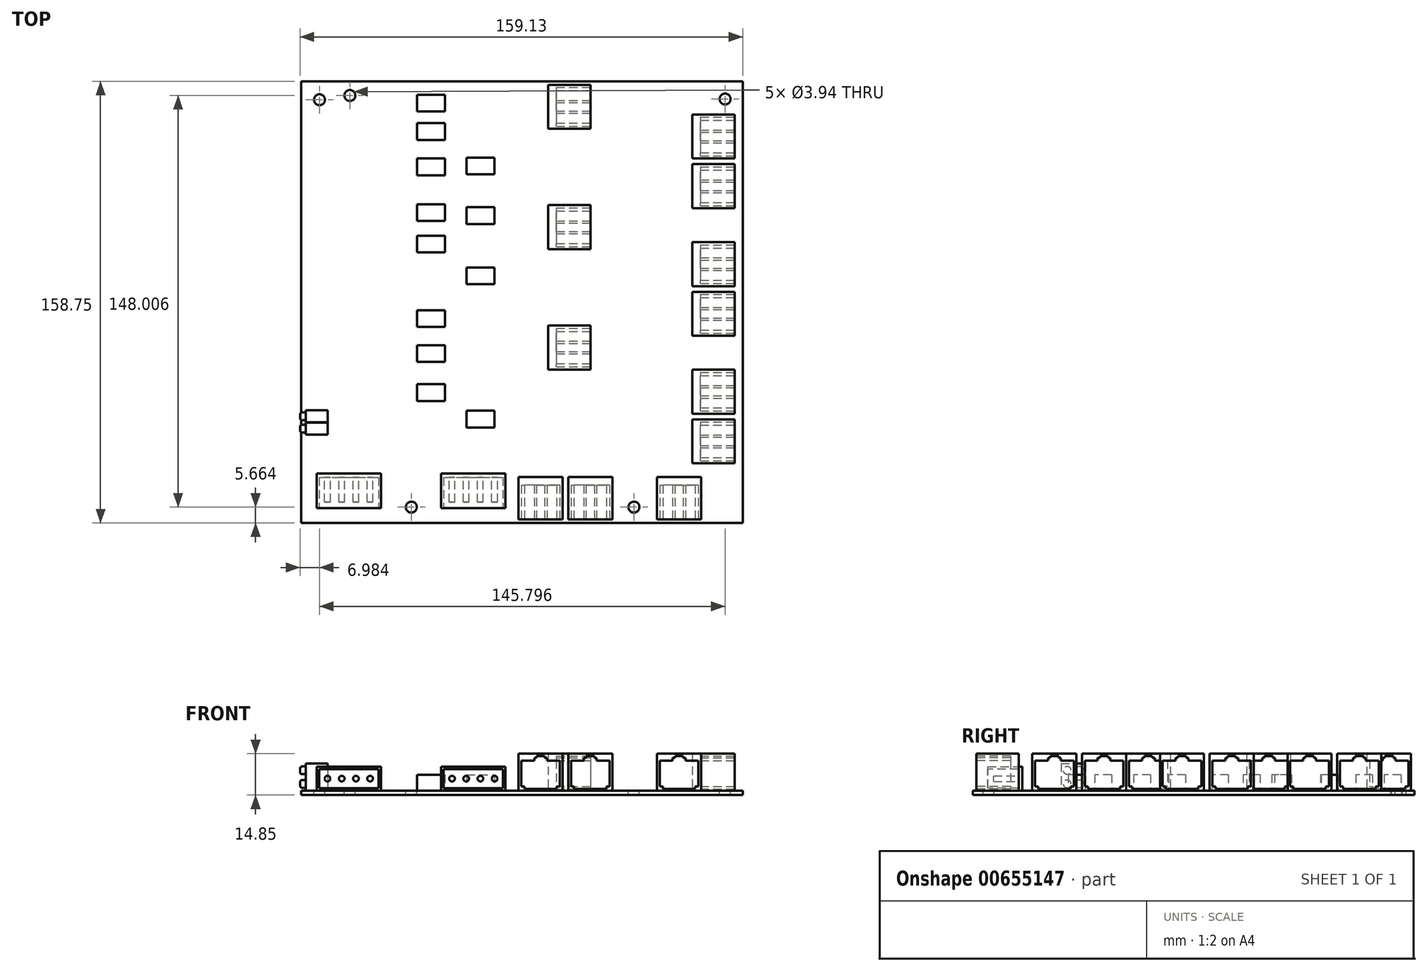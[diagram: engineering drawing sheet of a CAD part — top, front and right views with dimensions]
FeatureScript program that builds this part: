
annotation { "Feature Type Name" : "Feature", "Feature Type Description" : "" }
export const myFeature = defineFeature(function(context is Context, id is Id, definition is map)
    precondition{}
    {
        {
            var Q0;
            Q0=qCreatedBy(makeId("Top.planeOp"),FACE);
            var sketch = newSketch(context, id + "F0", { "sketchPlane" : qUnion([Q0])});
            skLineSegment(sketch, "E0.bottom", {"start": v(0, 0) * mm, "end": v(158.75, 0) * mm});
            skLineSegment(sketch, "E0.top", {"start": v(0, 158.75) * mm, "end": v(158.75, 158.75) * mm});
            skLineSegment(sketch, "E0.left", {"start": v(0, 0) * mm, "end": v(0, 158.75) * mm});
            skLineSegment(sketch, "E0.right", {"start": v(158.75, 0) * mm, "end": v(158.75, 158.75) * mm});
            skSolve(sketch);
        }
        {
            var Q0;
            Q0=makeQuery(id+"F0.imprint","IMPRINT",FACE,{"disambiguationData":[TD([[makeQuery(id+"F0.imprint","IMPRINT",EDGE,{"derivedFrom":sQuery(id+"F0.wireOp",EDGE,"E0.bottom")}),1.0]])]});
            extrude(context, id + "F1", {"entities" : qUnion([Q0]), "depth" : 1.59 * mm, "offsetDistance" : 25.4 * mm});
        }
        {
            var Q0;
            Q0=makeQuery(id+"F1.opExtrude","CAP_FACE",FACE,{"disambiguationData":[OSD([sQuery(id+"F0.wireOp",EDGE,"E0.bottom"),sQuery(id+"F0.wireOp",EDGE,"E0.top"),sQuery(id+"F0.wireOp",EDGE,"E0.left"),sQuery(id+"F0.wireOp",EDGE,"E0.right")])],"isStart":false});
            var sketch = newSketch(context, id + "F2", { "sketchPlane" : qUnion([Q0])});
            skCircle(sketch, "E1", {"center": v(119.63, 5.66) * mm, "radius": 1.97 * mm});
            skCircle(sketch, "E2", {"center": v(39.62, 5.66) * mm, "radius": 1.97 * mm});
            skCircle(sketch, "E3", {"center": v(152.4, 152.4) * mm, "radius": 1.97 * mm});
            skCircle(sketch, "E4", {"center": v(17.53, 153.67) * mm, "radius": 1.97 * mm});
            skCircle(sketch, "E5", {"center": v(6.6, 152.15) * mm, "radius": 1.97 * mm});
            skSolve(sketch);
        }
        {
            var Q0;
            Q0 = qSketchRegion(id + "F2", true);
            extrude(context, id + "F3", {"entities" : qUnion([Q0]), "operationType" : NewBodyOperationType.REMOVE, "endBound" : BoundingType.UP_TO_NEXT, "oppositeDirection" : true, "depth" : 25.4 * mm, "offsetDistance" : 25.4 * mm});
        }
        {
            var Q0;
            Q0=makeQuery(id+"F1.opExtrude","CAP_FACE",FACE,{"disambiguationData":[OSD([sQuery(id+"F0.wireOp",EDGE,"E0.bottom"),sQuery(id+"F0.wireOp",EDGE,"E0.top"),sQuery(id+"F0.wireOp",EDGE,"E0.left"),sQuery(id+"F0.wireOp",EDGE,"E0.right")])],"isStart":false});
            var sketch = newSketch(context, id + "F4", { "sketchPlane" : qUnion([Q0])});
            skLineSegment(sketch, "E6.bottom", {"start": v(140.61, 21.39) * mm, "end": v(155.85, 21.39) * mm});
            skLineSegment(sketch, "E6.top", {"start": v(140.61, 37.21) * mm, "end": v(155.85, 37.21) * mm});
            skLineSegment(sketch, "E6.left", {"start": v(140.61, 21.39) * mm, "end": v(140.61, 37.21) * mm});
            skLineSegment(sketch, "E6.right", {"start": v(155.85, 21.39) * mm, "end": v(155.85, 37.21) * mm});
            skLineSegment(sketch, "E7.bottom", {"start": v(140.61, 39.24) * mm, "end": v(155.85, 39.24) * mm});
            skLineSegment(sketch, "E7.top", {"start": v(140.61, 55.07) * mm, "end": v(155.85, 55.07) * mm});
            skLineSegment(sketch, "E7.left", {"start": v(140.61, 39.24) * mm, "end": v(140.61, 55.07) * mm});
            skLineSegment(sketch, "E7.right", {"start": v(155.85, 39.24) * mm, "end": v(155.85, 55.07) * mm});
            skLineSegment(sketch, "E8.bottom", {"start": v(140.61, 67.26) * mm, "end": v(155.85, 67.26) * mm});
            skLineSegment(sketch, "E8.top", {"start": v(140.61, 83.08) * mm, "end": v(155.85, 83.08) * mm});
            skLineSegment(sketch, "E8.left", {"start": v(140.61, 67.26) * mm, "end": v(140.61, 83.08) * mm});
            skLineSegment(sketch, "E8.right", {"start": v(155.85, 67.26) * mm, "end": v(155.85, 83.08) * mm});
            skLineSegment(sketch, "E9.bottom", {"start": v(140.61, 85.12) * mm, "end": v(155.85, 85.12) * mm});
            skLineSegment(sketch, "E9.top", {"start": v(140.61, 100.94) * mm, "end": v(155.85, 100.94) * mm});
            skLineSegment(sketch, "E9.left", {"start": v(140.61, 85.12) * mm, "end": v(140.61, 100.94) * mm});
            skLineSegment(sketch, "E9.right", {"start": v(155.85, 85.12) * mm, "end": v(155.85, 100.94) * mm});
            skLineSegment(sketch, "E10.bottom", {"start": v(140.61, 113.13) * mm, "end": v(155.85, 113.13) * mm});
            skLineSegment(sketch, "E10.top", {"start": v(140.61, 128.96) * mm, "end": v(155.85, 128.96) * mm});
            skLineSegment(sketch, "E10.left", {"start": v(140.61, 113.13) * mm, "end": v(140.61, 128.96) * mm});
            skLineSegment(sketch, "E10.right", {"start": v(155.85, 113.13) * mm, "end": v(155.85, 128.96) * mm});
            skLineSegment(sketch, "E11.bottom", {"start": v(140.61, 130.99) * mm, "end": v(155.85, 130.99) * mm});
            skLineSegment(sketch, "E11.top", {"start": v(140.61, 146.81) * mm, "end": v(155.85, 146.81) * mm});
            skLineSegment(sketch, "E11.left", {"start": v(140.61, 130.99) * mm, "end": v(140.61, 146.81) * mm});
            skLineSegment(sketch, "E11.right", {"start": v(155.85, 130.99) * mm, "end": v(155.85, 146.81) * mm});
            skLineSegment(sketch, "E12.bottom", {"start": v(127.94, 1.27) * mm, "end": v(143.76, 1.27) * mm});
            skLineSegment(sketch, "E12.top", {"start": v(127.94, 16.51) * mm, "end": v(143.76, 16.51) * mm});
            skLineSegment(sketch, "E12.left", {"start": v(127.94, 1.27) * mm, "end": v(127.94, 16.51) * mm});
            skLineSegment(sketch, "E12.right", {"start": v(143.76, 1.27) * mm, "end": v(143.76, 16.51) * mm});
            skLineSegment(sketch, "E13.bottom", {"start": v(111.86, 1.27) * mm, "end": v(96.04, 1.27) * mm});
            skLineSegment(sketch, "E13.top", {"start": v(111.86, 16.51) * mm, "end": v(96.04, 16.51) * mm});
            skLineSegment(sketch, "E13.left", {"start": v(111.86, 1.27) * mm, "end": v(111.86, 16.51) * mm});
            skLineSegment(sketch, "E13.right", {"start": v(96.04, 1.27) * mm, "end": v(96.04, 16.51) * mm});
            skLineSegment(sketch, "E14.bottom", {"start": v(94, 1.27) * mm, "end": v(78.18, 1.27) * mm});
            skLineSegment(sketch, "E14.top", {"start": v(94, 16.51) * mm, "end": v(78.18, 16.51) * mm});
            skLineSegment(sketch, "E14.left", {"start": v(94, 1.27) * mm, "end": v(94, 16.51) * mm});
            skLineSegment(sketch, "E14.right", {"start": v(78.18, 1.27) * mm, "end": v(78.18, 16.51) * mm});
            skLineSegment(sketch, "E15.bottom", {"start": v(88.82, 157.48) * mm, "end": v(104.06, 157.48) * mm});
            skLineSegment(sketch, "E15.top", {"start": v(88.82, 141.66) * mm, "end": v(104.06, 141.66) * mm});
            skLineSegment(sketch, "E15.left", {"start": v(88.82, 157.48) * mm, "end": v(88.82, 141.66) * mm});
            skLineSegment(sketch, "E15.right", {"start": v(104.06, 157.48) * mm, "end": v(104.06, 141.66) * mm});
            skLineSegment(sketch, "E16.bottom", {"start": v(88.82, 114.22) * mm, "end": v(104.06, 114.22) * mm});
            skLineSegment(sketch, "E16.top", {"start": v(88.82, 98.4) * mm, "end": v(104.06, 98.4) * mm});
            skLineSegment(sketch, "E16.left", {"start": v(88.82, 114.22) * mm, "end": v(88.82, 98.4) * mm});
            skLineSegment(sketch, "E16.right", {"start": v(104.06, 114.22) * mm, "end": v(104.06, 98.4) * mm});
            skLineSegment(sketch, "E17.bottom", {"start": v(88.82, 70.97) * mm, "end": v(104.06, 70.97) * mm});
            skLineSegment(sketch, "E17.top", {"start": v(88.82, 55.14) * mm, "end": v(104.06, 55.14) * mm});
            skLineSegment(sketch, "E17.left", {"start": v(88.82, 70.97) * mm, "end": v(88.82, 55.14) * mm});
            skLineSegment(sketch, "E17.right", {"start": v(104.06, 70.97) * mm, "end": v(104.06, 55.14) * mm});
            skSolve(sketch);
        }
        {
            var Q0;
            Q0 = qSketchRegion(id + "F4", true);
            extrude(context, id + "F5", {"entities" : qUnion([Q0]), "operationType" : NewBodyOperationType.ADD, "depth" : 13.26 * mm, "offsetDistance" : 25.4 * mm});
        }
        {
            var Q0;
            Q0=makeQuery(id+"F5.opExtrude","SWEPT_FACE",FACE,{"disambiguationData":[OSD([sQuery(id+"F4.wireOp",EDGE,"E6.right")])]});
            var sketch = newSketch(context, id + "F6", { "sketchPlane" : qUnion([Q0])});
            skLineSegment(sketch, "E18", {"start": v(29.3, 13.98) * mm, "end": v(30.79, 13.98) * mm});
            skPoint(sketch, "E18.startSnap0", {"position": v(29.3, 14.85) * mm});
            skLineSegment(sketch, "E19", {"start": v(30.79, 13.98) * mm, "end": v(30.79, 13.32) * mm});
            skLineSegment(sketch, "E20", {"start": v(30.79, 13.32) * mm, "end": v(31.6, 13.32) * mm});
            skLineSegment(sketch, "E21", {"start": v(31.6, 13.32) * mm, "end": v(31.6, 12.4) * mm});
            skLineSegment(sketch, "E22", {"start": v(31.6, 12.4) * mm, "end": v(36.25, 12.4) * mm});
            skLineSegment(sketch, "E23", {"start": v(36.25, 12.4) * mm, "end": v(36.25, 3.14) * mm});
            skLineSegment(sketch, "E24", {"start": v(36.25, 3.14) * mm, "end": v(35.12, 3.14) * mm});
            skLineSegment(sketch, "E25", {"start": v(35.12, 3.14) * mm, "end": v(35.12, 2.16) * mm});
            skLineSegment(sketch, "E26", {"start": v(35.12, 2.16) * mm, "end": v(29.3, 2.16) * mm});
            skLineSegment(sketch, "E27.MirrorCS", {"start": v(23.47, 3.14) * mm, "end": v(23.47, 2.16) * mm});
            skLineSegment(sketch, "E28.MirrorCS", {"start": v(22.35, 3.14) * mm, "end": v(23.47, 3.14) * mm});
            skLineSegment(sketch, "E29.MirrorCS", {"start": v(27, 13.32) * mm, "end": v(27, 12.4) * mm});
            skLineSegment(sketch, "E30.MirrorCS", {"start": v(27.8, 13.32) * mm, "end": v(27, 13.32) * mm});
            skLineSegment(sketch, "E31.MirrorCS", {"start": v(27.8, 13.98) * mm, "end": v(27.8, 13.32) * mm});
            skLineSegment(sketch, "E32.MirrorCS", {"start": v(23.47, 2.16) * mm, "end": v(29.3, 2.16) * mm});
            skLineSegment(sketch, "E33.MirrorCS", {"start": v(22.35, 12.4) * mm, "end": v(22.35, 3.14) * mm});
            skLineSegment(sketch, "E34.MirrorCS", {"start": v(29.3, 13.98) * mm, "end": v(27.8, 13.98) * mm});
            skLineSegment(sketch, "E35.MirrorCS", {"start": v(27, 12.4) * mm, "end": v(22.35, 12.4) * mm});
            skSolve(sketch);
        }
        {
            var Q0;
            Q0=makeQuery(id+"F6.imprint","IMPRINT",FACE,{"disambiguationData":[TD([[makeQuery(id+"F6.imprint","IMPRINT",EDGE,{"derivedFrom":sQuery(id+"F6.wireOp",EDGE,"E18")}),-1.0]])]});
            extrude(context, id + "F7", {"entities" : qUnion([Q0]), "operationType" : NewBodyOperationType.REMOVE, "oppositeDirection" : true, "depth" : 12.32 * mm, "offsetDistance" : 25.4 * mm});
        }
        {
            var Q0;
            Q0=makeQuery(id+"F5.opExtrude","SWEPT_FACE",FACE,{"disambiguationData":[OSD([sQuery(id+"F4.wireOp",EDGE,"E7.right")])]});
            var sketch = newSketch(context, id + "F8", { "sketchPlane" : qUnion([Q0])});
            skLineSegment(sketch, "E36", {"start": v(47.16, 13.98) * mm, "end": v(48.64, 13.98) * mm});
            skPoint(sketch, "E36.startSnap0", {"position": v(47.16, 14.85) * mm});
            skLineSegment(sketch, "E37", {"start": v(48.64, 13.98) * mm, "end": v(48.64, 13.32) * mm});
            skLineSegment(sketch, "E38", {"start": v(48.64, 13.32) * mm, "end": v(49.45, 13.32) * mm});
            skLineSegment(sketch, "E39", {"start": v(49.45, 13.32) * mm, "end": v(49.45, 12.4) * mm});
            skLineSegment(sketch, "E40", {"start": v(49.45, 12.4) * mm, "end": v(54.1, 12.4) * mm});
            skLineSegment(sketch, "E41", {"start": v(54.1, 12.4) * mm, "end": v(54.1, 3.14) * mm});
            skLineSegment(sketch, "E42", {"start": v(54.1, 3.14) * mm, "end": v(52.98, 3.14) * mm});
            skLineSegment(sketch, "E43", {"start": v(52.98, 3.14) * mm, "end": v(52.98, 2.16) * mm});
            skLineSegment(sketch, "E44", {"start": v(52.98, 2.16) * mm, "end": v(47.16, 2.16) * mm});
            skPoint(sketch, "E45.endSnap0", {"position": v(47.16, 1.59) * mm});
            skLineSegment(sketch, "E46.MirrorCS", {"start": v(41.33, 2.16) * mm, "end": v(47.16, 2.16) * mm});
            skLineSegment(sketch, "E47.MirrorCS", {"start": v(41.33, 3.14) * mm, "end": v(41.33, 2.16) * mm});
            skLineSegment(sketch, "E48.MirrorCS", {"start": v(44.86, 12.4) * mm, "end": v(40.2, 12.4) * mm});
            skLineSegment(sketch, "E49.MirrorCS", {"start": v(44.86, 13.32) * mm, "end": v(44.86, 12.4) * mm});
            skLineSegment(sketch, "E50.MirrorCS", {"start": v(47.16, 13.98) * mm, "end": v(45.67, 13.98) * mm});
            skLineSegment(sketch, "E51.MirrorCS", {"start": v(45.67, 13.98) * mm, "end": v(45.67, 13.32) * mm});
            skLineSegment(sketch, "E52.MirrorCS", {"start": v(45.67, 13.32) * mm, "end": v(44.86, 13.32) * mm});
            skLineSegment(sketch, "E53.MirrorCS", {"start": v(40.2, 12.4) * mm, "end": v(40.2, 3.14) * mm});
            skLineSegment(sketch, "E54.MirrorCS", {"start": v(40.2, 3.14) * mm, "end": v(41.33, 3.14) * mm});
            skLineSegment(sketch, "E55", {"start": v(73.68, 13.98) * mm, "end": v(76.66, 13.98) * mm});
            skPoint(sketch, "E55.startSnap0", {"position": v(75.17, 14.85) * mm});
            skLineSegment(sketch, "E56", {"start": v(76.66, 13.98) * mm, "end": v(76.66, 13.32) * mm});
            skLineSegment(sketch, "E57", {"start": v(76.66, 13.32) * mm, "end": v(77.47, 13.32) * mm});
            skLineSegment(sketch, "E58", {"start": v(77.47, 13.32) * mm, "end": v(77.47, 12.4) * mm});
            skLineSegment(sketch, "E59", {"start": v(77.47, 12.4) * mm, "end": v(82.12, 12.4) * mm});
            skLineSegment(sketch, "E60", {"start": v(82.12, 12.4) * mm, "end": v(82.12, 3.14) * mm});
            skLineSegment(sketch, "E61", {"start": v(82.12, 3.14) * mm, "end": v(81, 3.14) * mm});
            skLineSegment(sketch, "E62", {"start": v(81, 3.14) * mm, "end": v(81, 2.16) * mm});
            skLineSegment(sketch, "E63", {"start": v(81, 2.16) * mm, "end": v(69.35, 2.16) * mm});
            skPoint(sketch, "E64.endSnap0", {"position": v(75.91, 1.22) * mm});
            skLineSegment(sketch, "E65.MirrorCS", {"start": v(69.35, 3.14) * mm, "end": v(69.35, 2.16) * mm});
            skLineSegment(sketch, "E66.MirrorCS", {"start": v(72.87, 12.4) * mm, "end": v(68.22, 12.4) * mm});
            skLineSegment(sketch, "E67.MirrorCS", {"start": v(72.87, 13.32) * mm, "end": v(72.87, 12.4) * mm});
            skLineSegment(sketch, "E68.MirrorCS", {"start": v(73.68, 13.98) * mm, "end": v(73.68, 13.32) * mm});
            skLineSegment(sketch, "E69.MirrorCS", {"start": v(73.68, 13.32) * mm, "end": v(72.87, 13.32) * mm});
            skLineSegment(sketch, "E70.MirrorCS", {"start": v(68.22, 12.4) * mm, "end": v(68.22, 3.14) * mm});
            skLineSegment(sketch, "E71.MirrorCS", {"start": v(68.22, 3.14) * mm, "end": v(69.35, 3.14) * mm});
            skPoint(sketch, "E72.orphan", {"position": v(75.17, 13.98) * mm});
            skPoint(sketch, "E73.orphan", {"position": v(75.17, 2.16) * mm});
            skLineSegment(sketch, "E74", {"start": v(91.54, 13.98) * mm, "end": v(94.52, 13.98) * mm});
            skPoint(sketch, "E74.startSnap0", {"position": v(93.03, 14.85) * mm});
            skLineSegment(sketch, "E75", {"start": v(94.52, 13.98) * mm, "end": v(94.52, 13.32) * mm});
            skLineSegment(sketch, "E76", {"start": v(94.52, 13.32) * mm, "end": v(95.32, 13.32) * mm});
            skLineSegment(sketch, "E77", {"start": v(95.32, 13.32) * mm, "end": v(95.32, 12.4) * mm});
            skLineSegment(sketch, "E78", {"start": v(95.32, 12.4) * mm, "end": v(99.98, 12.4) * mm});
            skLineSegment(sketch, "E79", {"start": v(99.98, 12.4) * mm, "end": v(99.98, 3.14) * mm});
            skLineSegment(sketch, "E80", {"start": v(99.98, 3.14) * mm, "end": v(98.85, 3.14) * mm});
            skLineSegment(sketch, "E81", {"start": v(98.85, 3.14) * mm, "end": v(98.85, 2.16) * mm});
            skLineSegment(sketch, "E82", {"start": v(98.85, 2.16) * mm, "end": v(87.2, 2.16) * mm});
            skLineSegment(sketch, "E83.MirrorCS", {"start": v(87.2, 3.14) * mm, "end": v(87.2, 2.16) * mm});
            skLineSegment(sketch, "E84.MirrorCS", {"start": v(90.73, 12.4) * mm, "end": v(86.08, 12.4) * mm});
            skLineSegment(sketch, "E85.MirrorCS", {"start": v(90.73, 13.32) * mm, "end": v(90.73, 12.4) * mm});
            skLineSegment(sketch, "E86.MirrorCS", {"start": v(91.54, 13.98) * mm, "end": v(91.54, 13.32) * mm});
            skLineSegment(sketch, "E87.MirrorCS", {"start": v(91.54, 13.32) * mm, "end": v(90.73, 13.32) * mm});
            skLineSegment(sketch, "E88.MirrorCS", {"start": v(86.08, 12.4) * mm, "end": v(86.08, 3.14) * mm});
            skLineSegment(sketch, "E89.MirrorCS", {"start": v(86.08, 3.14) * mm, "end": v(87.2, 3.14) * mm});
            skPoint(sketch, "E90.orphan", {"position": v(93.03, 13.98) * mm});
            skPoint(sketch, "E91.orphan", {"position": v(93.03, 2.16) * mm});
            skLineSegment(sketch, "E92", {"start": v(119.55, 13.98) * mm, "end": v(122.53, 13.98) * mm});
            skPoint(sketch, "E92.startSnap0", {"position": v(121.04, 14.85) * mm});
            skLineSegment(sketch, "E93", {"start": v(122.53, 13.98) * mm, "end": v(122.53, 13.32) * mm});
            skLineSegment(sketch, "E94", {"start": v(122.53, 13.32) * mm, "end": v(123.34, 13.32) * mm});
            skLineSegment(sketch, "E95", {"start": v(123.34, 13.32) * mm, "end": v(123.34, 12.4) * mm});
            skLineSegment(sketch, "E96", {"start": v(123.34, 12.4) * mm, "end": v(128, 12.4) * mm});
            skLineSegment(sketch, "E97", {"start": v(128, 12.4) * mm, "end": v(128, 3.14) * mm});
            skLineSegment(sketch, "E98", {"start": v(128, 3.14) * mm, "end": v(126.87, 3.14) * mm});
            skLineSegment(sketch, "E99", {"start": v(126.87, 3.14) * mm, "end": v(126.87, 2.16) * mm});
            skLineSegment(sketch, "E100", {"start": v(126.87, 2.16) * mm, "end": v(115.22, 2.16) * mm});
            skLineSegment(sketch, "E101.MirrorCS", {"start": v(115.22, 3.14) * mm, "end": v(115.22, 2.16) * mm});
            skLineSegment(sketch, "E102.MirrorCS", {"start": v(118.75, 12.4) * mm, "end": v(114.1, 12.4) * mm});
            skLineSegment(sketch, "E103.MirrorCS", {"start": v(118.75, 13.32) * mm, "end": v(118.75, 12.4) * mm});
            skLineSegment(sketch, "E104.MirrorCS", {"start": v(119.55, 13.98) * mm, "end": v(119.55, 13.32) * mm});
            skLineSegment(sketch, "E105.MirrorCS", {"start": v(119.55, 13.32) * mm, "end": v(118.75, 13.32) * mm});
            skLineSegment(sketch, "E106.MirrorCS", {"start": v(114.1, 12.4) * mm, "end": v(114.1, 3.14) * mm});
            skLineSegment(sketch, "E107.MirrorCS", {"start": v(114.1, 3.14) * mm, "end": v(115.22, 3.14) * mm});
            skPoint(sketch, "E108.orphan", {"position": v(121.04, 13.98) * mm});
            skPoint(sketch, "E109.orphan", {"position": v(121.04, 2.16) * mm});
            skLineSegment(sketch, "E110", {"start": v(137.41, 13.98) * mm, "end": v(140.39, 13.98) * mm});
            skPoint(sketch, "E110.startSnap0", {"position": v(138.9, 14.85) * mm});
            skLineSegment(sketch, "E111", {"start": v(140.39, 13.98) * mm, "end": v(140.39, 13.32) * mm});
            skLineSegment(sketch, "E112", {"start": v(140.39, 13.32) * mm, "end": v(141.2, 13.32) * mm});
            skLineSegment(sketch, "E113", {"start": v(141.2, 13.32) * mm, "end": v(141.2, 12.4) * mm});
            skLineSegment(sketch, "E114", {"start": v(141.2, 12.4) * mm, "end": v(145.85, 12.4) * mm});
            skLineSegment(sketch, "E115", {"start": v(145.85, 12.4) * mm, "end": v(145.85, 3.14) * mm});
            skLineSegment(sketch, "E116", {"start": v(145.85, 3.14) * mm, "end": v(144.72, 3.14) * mm});
            skLineSegment(sketch, "E117", {"start": v(144.72, 3.14) * mm, "end": v(144.72, 2.16) * mm});
            skLineSegment(sketch, "E118", {"start": v(144.72, 2.16) * mm, "end": v(133.08, 2.16) * mm});
            skPoint(sketch, "E119.endSnap0", {"position": v(145.22, -24.66) * mm});
            skLineSegment(sketch, "E120.MirrorCS", {"start": v(133.08, 3.14) * mm, "end": v(133.08, 2.16) * mm});
            skLineSegment(sketch, "E121.MirrorCS", {"start": v(136.6, 12.4) * mm, "end": v(131.95, 12.4) * mm});
            skLineSegment(sketch, "E122.MirrorCS", {"start": v(136.6, 13.32) * mm, "end": v(136.6, 12.4) * mm});
            skLineSegment(sketch, "E123.MirrorCS", {"start": v(137.41, 13.98) * mm, "end": v(137.41, 13.32) * mm});
            skLineSegment(sketch, "E124.MirrorCS", {"start": v(137.41, 13.32) * mm, "end": v(136.6, 13.32) * mm});
            skLineSegment(sketch, "E125.MirrorCS", {"start": v(131.95, 12.4) * mm, "end": v(131.95, 3.14) * mm});
            skLineSegment(sketch, "E126.MirrorCS", {"start": v(131.95, 3.14) * mm, "end": v(133.08, 3.14) * mm});
            skPoint(sketch, "E127.orphan", {"position": v(138.9, 13.98) * mm});
            skPoint(sketch, "E128.orphan", {"position": v(138.9, 2.16) * mm});
            skSolve(sketch);
        }
        {
            var Q0;
            Q0 = qSketchRegion(id + "F8", true);
            extrude(context, id + "F9", {"entities" : qUnion([Q0]), "operationType" : NewBodyOperationType.REMOVE, "oppositeDirection" : true, "depth" : 12.32 * mm, "offsetDistance" : 25.4 * mm});
        }
        {
            var Q0;
            Q0=makeQuery(id+"F5.opExtrude","SWEPT_FACE",FACE,{"disambiguationData":[OSD([sQuery(id+"F4.wireOp",EDGE,"E17.right")])]});
            var sketch = newSketch(context, id + "F10", { "sketchPlane" : qUnion([Q0])});
            skLineSegment(sketch, "E129", {"start": v(61.57, 13.98) * mm, "end": v(64.54, 13.98) * mm});
            skPoint(sketch, "E129.startSnap0", {"position": v(63.06, 14.85) * mm});
            skLineSegment(sketch, "E130", {"start": v(64.54, 13.98) * mm, "end": v(64.54, 13.32) * mm});
            skLineSegment(sketch, "E131", {"start": v(64.54, 13.32) * mm, "end": v(65.35, 13.32) * mm});
            skLineSegment(sketch, "E132", {"start": v(65.35, 13.32) * mm, "end": v(65.35, 12.4) * mm});
            skLineSegment(sketch, "E133", {"start": v(65.35, 12.4) * mm, "end": v(70, 12.4) * mm});
            skLineSegment(sketch, "E134", {"start": v(70, 12.4) * mm, "end": v(70, 3.14) * mm});
            skLineSegment(sketch, "E135", {"start": v(70, 3.14) * mm, "end": v(68.88, 3.14) * mm});
            skLineSegment(sketch, "E136", {"start": v(68.88, 3.14) * mm, "end": v(68.88, 2.16) * mm});
            skLineSegment(sketch, "E137", {"start": v(68.88, 2.16) * mm, "end": v(57.23, 2.16) * mm});
            skLineSegment(sketch, "E138.MirrorCS", {"start": v(57.23, 3.14) * mm, "end": v(57.23, 2.16) * mm});
            skLineSegment(sketch, "E139.MirrorCS", {"start": v(60.76, 12.4) * mm, "end": v(56.1, 12.4) * mm});
            skLineSegment(sketch, "E140.MirrorCS", {"start": v(60.76, 13.32) * mm, "end": v(60.76, 12.4) * mm});
            skLineSegment(sketch, "E141.MirrorCS", {"start": v(61.57, 13.98) * mm, "end": v(61.57, 13.32) * mm});
            skLineSegment(sketch, "E142.MirrorCS", {"start": v(61.57, 13.32) * mm, "end": v(60.76, 13.32) * mm});
            skLineSegment(sketch, "E143.MirrorCS", {"start": v(56.1, 12.4) * mm, "end": v(56.1, 3.14) * mm});
            skLineSegment(sketch, "E144.MirrorCS", {"start": v(56.1, 3.14) * mm, "end": v(57.23, 3.14) * mm});
            skPoint(sketch, "E145.orphan", {"position": v(63.06, 13.98) * mm});
            skPoint(sketch, "E146.orphan", {"position": v(63.06, 2.16) * mm});
            skLineSegment(sketch, "E147", {"start": v(104.82, 13.98) * mm, "end": v(107.8, 13.98) * mm});
            skPoint(sketch, "E147.startSnap0", {"position": v(106.31, 14.85) * mm});
            skLineSegment(sketch, "E148", {"start": v(107.8, 13.98) * mm, "end": v(107.8, 13.32) * mm});
            skLineSegment(sketch, "E149", {"start": v(107.8, 13.32) * mm, "end": v(108.6, 13.32) * mm});
            skLineSegment(sketch, "E150", {"start": v(108.6, 13.32) * mm, "end": v(108.6, 12.4) * mm});
            skLineSegment(sketch, "E151", {"start": v(108.6, 12.4) * mm, "end": v(113.26, 12.4) * mm});
            skLineSegment(sketch, "E152", {"start": v(113.26, 12.4) * mm, "end": v(113.26, 3.14) * mm});
            skLineSegment(sketch, "E153", {"start": v(113.26, 3.14) * mm, "end": v(112.14, 3.14) * mm});
            skLineSegment(sketch, "E154", {"start": v(112.14, 3.14) * mm, "end": v(112.14, 2.16) * mm});
            skLineSegment(sketch, "E155", {"start": v(112.14, 2.16) * mm, "end": v(100.49, 2.16) * mm});
            skLineSegment(sketch, "E156.MirrorCS", {"start": v(100.49, 3.14) * mm, "end": v(100.49, 2.16) * mm});
            skLineSegment(sketch, "E157.MirrorCS", {"start": v(104.02, 12.4) * mm, "end": v(99.36, 12.4) * mm});
            skLineSegment(sketch, "E158.MirrorCS", {"start": v(104.02, 13.32) * mm, "end": v(104.02, 12.4) * mm});
            skLineSegment(sketch, "E159.MirrorCS", {"start": v(104.82, 13.98) * mm, "end": v(104.82, 13.32) * mm});
            skLineSegment(sketch, "E160.MirrorCS", {"start": v(104.82, 13.32) * mm, "end": v(104.02, 13.32) * mm});
            skLineSegment(sketch, "E161.MirrorCS", {"start": v(99.36, 12.4) * mm, "end": v(99.36, 3.14) * mm});
            skLineSegment(sketch, "E162.MirrorCS", {"start": v(99.36, 3.14) * mm, "end": v(100.49, 3.14) * mm});
            skPoint(sketch, "E163.orphan", {"position": v(106.31, 13.98) * mm});
            skPoint(sketch, "E164.orphan", {"position": v(106.31, 2.16) * mm});
            skLineSegment(sketch, "E165", {"start": v(148.08, 13.98) * mm, "end": v(151.06, 13.98) * mm});
            skPoint(sketch, "E165.startSnap0", {"position": v(149.57, 14.85) * mm});
            skLineSegment(sketch, "E166", {"start": v(151.06, 13.98) * mm, "end": v(151.06, 13.32) * mm});
            skLineSegment(sketch, "E167", {"start": v(151.06, 13.32) * mm, "end": v(151.86, 13.32) * mm});
            skLineSegment(sketch, "E168", {"start": v(151.86, 13.32) * mm, "end": v(151.86, 12.4) * mm});
            skLineSegment(sketch, "E169", {"start": v(151.86, 12.4) * mm, "end": v(156.52, 12.4) * mm});
            skLineSegment(sketch, "E170", {"start": v(156.52, 12.4) * mm, "end": v(156.52, 3.14) * mm});
            skLineSegment(sketch, "E171", {"start": v(156.52, 3.14) * mm, "end": v(155.4, 3.14) * mm});
            skLineSegment(sketch, "E172", {"start": v(155.4, 3.14) * mm, "end": v(155.4, 2.16) * mm});
            skLineSegment(sketch, "E173", {"start": v(155.4, 2.16) * mm, "end": v(143.74, 2.16) * mm});
            skLineSegment(sketch, "E174.MirrorCS", {"start": v(143.74, 3.14) * mm, "end": v(143.74, 2.16) * mm});
            skLineSegment(sketch, "E175.MirrorCS", {"start": v(147.27, 12.4) * mm, "end": v(142.62, 12.4) * mm});
            skLineSegment(sketch, "E176.MirrorCS", {"start": v(147.27, 13.32) * mm, "end": v(147.27, 12.4) * mm});
            skLineSegment(sketch, "E177.MirrorCS", {"start": v(148.08, 13.98) * mm, "end": v(148.08, 13.32) * mm});
            skLineSegment(sketch, "E178.MirrorCS", {"start": v(148.08, 13.32) * mm, "end": v(147.27, 13.32) * mm});
            skLineSegment(sketch, "E179.MirrorCS", {"start": v(142.62, 12.4) * mm, "end": v(142.62, 3.14) * mm});
            skLineSegment(sketch, "E180.MirrorCS", {"start": v(142.62, 3.14) * mm, "end": v(143.74, 3.14) * mm});
            skPoint(sketch, "E181.orphan", {"position": v(149.57, 13.98) * mm});
            skPoint(sketch, "E182.orphan", {"position": v(149.57, 2.16) * mm});
            skSolve(sketch);
        }
        {
            var Q0;
            Q0 = qSketchRegion(id + "F10", true);
            extrude(context, id + "F11", {"entities" : qUnion([Q0]), "operationType" : NewBodyOperationType.REMOVE, "oppositeDirection" : true, "depth" : 12.32 * mm, "offsetDistance" : 25.4 * mm});
        }
        {
            var Q0;
            Q0=makeQuery(id+"F5.opExtrude","SWEPT_FACE",FACE,{"disambiguationData":[OSD([sQuery(id+"F4.wireOp",EDGE,"E12.bottom")])]});
            var sketch = newSketch(context, id + "F12", { "sketchPlane" : qUnion([Q0])});
            skLineSegment(sketch, "E183", {"start": v(134.36, 13.98) * mm, "end": v(137.34, 13.98) * mm});
            skPoint(sketch, "E183.startSnap0", {"position": v(135.85, 14.85) * mm});
            skLineSegment(sketch, "E184", {"start": v(137.34, 13.98) * mm, "end": v(137.34, 13.32) * mm});
            skLineSegment(sketch, "E185", {"start": v(137.34, 13.32) * mm, "end": v(138.15, 13.32) * mm});
            skLineSegment(sketch, "E186", {"start": v(138.15, 13.32) * mm, "end": v(138.15, 12.4) * mm});
            skLineSegment(sketch, "E187", {"start": v(138.15, 12.4) * mm, "end": v(142.8, 12.4) * mm});
            skLineSegment(sketch, "E188", {"start": v(142.8, 12.4) * mm, "end": v(142.8, 3.14) * mm});
            skLineSegment(sketch, "E189", {"start": v(142.8, 3.14) * mm, "end": v(141.68, 3.14) * mm});
            skLineSegment(sketch, "E190", {"start": v(141.68, 3.14) * mm, "end": v(141.68, 2.16) * mm});
            skLineSegment(sketch, "E191", {"start": v(141.68, 2.16) * mm, "end": v(130.03, 2.16) * mm});
            skLineSegment(sketch, "E192.MirrorCS", {"start": v(130.03, 3.14) * mm, "end": v(130.03, 2.16) * mm});
            skLineSegment(sketch, "E193.MirrorCS", {"start": v(133.56, 12.4) * mm, "end": v(128.9, 12.4) * mm});
            skLineSegment(sketch, "E194.MirrorCS", {"start": v(133.56, 13.32) * mm, "end": v(133.56, 12.4) * mm});
            skLineSegment(sketch, "E195.MirrorCS", {"start": v(134.36, 13.98) * mm, "end": v(134.36, 13.32) * mm});
            skLineSegment(sketch, "E196.MirrorCS", {"start": v(134.36, 13.32) * mm, "end": v(133.56, 13.32) * mm});
            skLineSegment(sketch, "E197.MirrorCS", {"start": v(128.9, 12.4) * mm, "end": v(128.9, 3.14) * mm});
            skLineSegment(sketch, "E198.MirrorCS", {"start": v(128.9, 3.14) * mm, "end": v(130.03, 3.14) * mm});
            skPoint(sketch, "E199.orphan", {"position": v(135.85, 13.98) * mm});
            skPoint(sketch, "E200.orphan", {"position": v(135.85, 2.16) * mm});
            skLineSegment(sketch, "E201", {"start": v(102.46, 13.98) * mm, "end": v(105.44, 13.98) * mm});
            skPoint(sketch, "E201.startSnap0", {"position": v(103.95, 14.85) * mm});
            skLineSegment(sketch, "E202", {"start": v(105.44, 13.98) * mm, "end": v(105.44, 13.32) * mm});
            skLineSegment(sketch, "E203", {"start": v(105.44, 13.32) * mm, "end": v(106.25, 13.32) * mm});
            skLineSegment(sketch, "E204", {"start": v(106.25, 13.32) * mm, "end": v(106.25, 12.4) * mm});
            skLineSegment(sketch, "E205", {"start": v(106.25, 12.4) * mm, "end": v(110.9, 12.4) * mm});
            skLineSegment(sketch, "E206", {"start": v(110.9, 12.4) * mm, "end": v(110.9, 3.14) * mm});
            skLineSegment(sketch, "E207", {"start": v(110.9, 3.14) * mm, "end": v(109.77, 3.14) * mm});
            skLineSegment(sketch, "E208", {"start": v(109.77, 3.14) * mm, "end": v(109.77, 2.16) * mm});
            skLineSegment(sketch, "E209", {"start": v(109.77, 2.16) * mm, "end": v(98.13, 2.16) * mm});
            skLineSegment(sketch, "E210.MirrorCS", {"start": v(98.13, 3.14) * mm, "end": v(98.13, 2.16) * mm});
            skLineSegment(sketch, "E211.MirrorCS", {"start": v(101.65, 12.4) * mm, "end": v(97, 12.4) * mm});
            skLineSegment(sketch, "E212.MirrorCS", {"start": v(101.65, 13.32) * mm, "end": v(101.65, 12.4) * mm});
            skLineSegment(sketch, "E213.MirrorCS", {"start": v(102.46, 13.98) * mm, "end": v(102.46, 13.32) * mm});
            skLineSegment(sketch, "E214.MirrorCS", {"start": v(102.46, 13.32) * mm, "end": v(101.65, 13.32) * mm});
            skLineSegment(sketch, "E215.MirrorCS", {"start": v(97, 12.4) * mm, "end": v(97, 3.14) * mm});
            skLineSegment(sketch, "E216.MirrorCS", {"start": v(97, 3.14) * mm, "end": v(98.13, 3.14) * mm});
            skPoint(sketch, "E217.orphan", {"position": v(103.95, 13.98) * mm});
            skPoint(sketch, "E218.orphan", {"position": v(103.95, 2.16) * mm});
            skLineSegment(sketch, "E219", {"start": v(84.6, 13.98) * mm, "end": v(87.58, 13.98) * mm});
            skPoint(sketch, "E219.startSnap0", {"position": v(86.1, 14.85) * mm});
            skLineSegment(sketch, "E220", {"start": v(87.58, 13.98) * mm, "end": v(87.58, 13.32) * mm});
            skLineSegment(sketch, "E221", {"start": v(87.58, 13.32) * mm, "end": v(88.39, 13.32) * mm});
            skLineSegment(sketch, "E222", {"start": v(88.39, 13.32) * mm, "end": v(88.39, 12.4) * mm});
            skLineSegment(sketch, "E223", {"start": v(88.39, 12.4) * mm, "end": v(93.04, 12.4) * mm});
            skLineSegment(sketch, "E224", {"start": v(93.04, 12.4) * mm, "end": v(93.04, 3.14) * mm});
            skLineSegment(sketch, "E225", {"start": v(93.04, 3.14) * mm, "end": v(91.92, 3.14) * mm});
            skLineSegment(sketch, "E226", {"start": v(91.92, 3.14) * mm, "end": v(91.92, 2.16) * mm});
            skLineSegment(sketch, "E227", {"start": v(91.92, 2.16) * mm, "end": v(80.27, 2.16) * mm});
            skLineSegment(sketch, "E228.MirrorCS", {"start": v(80.27, 3.14) * mm, "end": v(80.27, 2.16) * mm});
            skLineSegment(sketch, "E229.MirrorCS", {"start": v(83.8, 12.4) * mm, "end": v(79.14, 12.4) * mm});
            skLineSegment(sketch, "E230.MirrorCS", {"start": v(83.8, 13.32) * mm, "end": v(83.8, 12.4) * mm});
            skLineSegment(sketch, "E231.MirrorCS", {"start": v(84.6, 13.98) * mm, "end": v(84.6, 13.32) * mm});
            skLineSegment(sketch, "E232.MirrorCS", {"start": v(84.6, 13.32) * mm, "end": v(83.8, 13.32) * mm});
            skLineSegment(sketch, "E233.MirrorCS", {"start": v(79.14, 12.4) * mm, "end": v(79.14, 3.14) * mm});
            skLineSegment(sketch, "E234.MirrorCS", {"start": v(79.14, 3.14) * mm, "end": v(80.27, 3.14) * mm});
            skPoint(sketch, "E235.orphan", {"position": v(86.1, 13.98) * mm});
            skPoint(sketch, "E236.orphan", {"position": v(86.1, 2.16) * mm});
            skSolve(sketch);
        }
        {
            var Q0;
            Q0 = qSketchRegion(id + "F12", true);
            extrude(context, id + "F13", {"entities" : qUnion([Q0]), "operationType" : NewBodyOperationType.REMOVE, "oppositeDirection" : true, "depth" : 12.32 * mm, "offsetDistance" : 25.4 * mm});
        }
        {
            var Q0;
            Q0=makeQuery(id+"F1.opExtrude","CAP_FACE",FACE,{"disambiguationData":[OSD([sQuery(id+"F0.wireOp",EDGE,"E0.bottom"),sQuery(id+"F0.wireOp",EDGE,"E0.top"),sQuery(id+"F0.wireOp",EDGE,"E0.left"),sQuery(id+"F0.wireOp",EDGE,"E0.right")])],"isStart":false});
            var sketch = newSketch(context, id + "F14", { "sketchPlane" : qUnion([Q0])});
            skLineSegment(sketch, "E237.bottom", {"start": v(50.32, 5.33) * mm, "end": v(73.48, 5.33) * mm});
            skLineSegment(sketch, "E237.top", {"start": v(50.32, 17.78) * mm, "end": v(73.48, 17.78) * mm});
            skLineSegment(sketch, "E237.left", {"start": v(50.32, 5.33) * mm, "end": v(50.32, 17.78) * mm});
            skLineSegment(sketch, "E237.right", {"start": v(73.48, 5.33) * mm, "end": v(73.48, 17.78) * mm});
            skLineSegment(sketch, "E238.bottom", {"start": v(28.73, 5.33) * mm, "end": v(5.56, 5.33) * mm});
            skLineSegment(sketch, "E238.top", {"start": v(28.73, 17.78) * mm, "end": v(5.56, 17.78) * mm});
            skLineSegment(sketch, "E238.left", {"start": v(28.73, 5.33) * mm, "end": v(28.73, 17.78) * mm});
            skLineSegment(sketch, "E238.right", {"start": v(5.56, 5.33) * mm, "end": v(5.56, 17.78) * mm});
            skSolve(sketch);
        }
        {
            var Q0;
            Q0 = qSketchRegion(id + "F14", true);
            extrude(context, id + "F15", {"entities" : qUnion([Q0]), "operationType" : NewBodyOperationType.ADD, "depth" : 8.64 * mm, "offsetDistance" : 25.4 * mm});
        }
        {
            var Q0;
            Q0=makeQuery(id+"F15.opExtrude","SWEPT_FACE",FACE,{"disambiguationData":[OSD([sQuery(id+"F14.wireOp",EDGE,"E237.bottom")])]});
            var sketch = newSketch(context, id + "F16", { "sketchPlane" : qUnion([Q0])});
            skLineSegment(sketch, "E239.bottom", {"start": v(51.2, 2.48) * mm, "end": v(72.6, 2.48) * mm});
            skLineSegment(sketch, "E239.top", {"start": v(51.2, 9.33) * mm, "end": v(72.6, 9.33) * mm});
            skLineSegment(sketch, "E239.left", {"start": v(51.2, 2.48) * mm, "end": v(51.2, 9.33) * mm});
            skLineSegment(sketch, "E239.right", {"start": v(72.6, 2.48) * mm, "end": v(72.6, 9.33) * mm});
            skLineSegment(sketch, "E240.bottom", {"start": v(6.45, 2.48) * mm, "end": v(27.84, 2.48) * mm});
            skLineSegment(sketch, "E240.top", {"start": v(6.45, 9.33) * mm, "end": v(27.84, 9.33) * mm});
            skLineSegment(sketch, "E240.left", {"start": v(6.45, 2.48) * mm, "end": v(6.45, 9.33) * mm});
            skLineSegment(sketch, "E240.right", {"start": v(27.84, 2.48) * mm, "end": v(27.84, 9.33) * mm});
            skSolve(sketch);
        }
        {
            var Q0;
            Q0 = qSketchRegion(id + "F16", true);
            extrude(context, id + "F17", {"entities" : qUnion([Q0]), "operationType" : NewBodyOperationType.REMOVE, "oppositeDirection" : true, "depth" : 11.05 * mm, "offsetDistance" : 25.4 * mm});
        }
        {
            var Q0;
            Q0=makeQuery(id+"F17.boolean.opBoolean","COPY",FACE,{"derivedFrom":makeQuery(id+"F17.opExtrude","CAP_FACE",FACE,{"disambiguationData":[OSD([sQuery(id+"F16.wireOp",EDGE,"E239.bottom"),sQuery(id+"F16.wireOp",EDGE,"E239.top"),sQuery(id+"F16.wireOp",EDGE,"E239.left"),sQuery(id+"F16.wireOp",EDGE,"E239.right")])],"isStart":false})});
            var sketch = newSketch(context, id + "F18", { "sketchPlane" : qUnion([Q0])});
            skPoint(sketch, "E241.startSnap0", {"position": v(51.2, 5.9) * mm});
            skCircle(sketch, "E242", {"center": v(54.25, 5.9) * mm, "radius": 1.02 * mm});
            skCircle(sketch, "E243", {"center": v(59.36, 5.9) * mm, "radius": 1.02 * mm});
            skCircle(sketch, "E244", {"center": v(64.47, 5.9) * mm, "radius": 1.02 * mm});
            skCircle(sketch, "E245", {"center": v(69.57, 5.9) * mm, "radius": 1.02 * mm});
            skPoint(sketch, "E246.startSnap0", {"position": v(6.45, 5.9) * mm});
            skCircle(sketch, "E247", {"center": v(9.5, 5.9) * mm, "radius": 1.02 * mm});
            skCircle(sketch, "E248", {"center": v(14.6, 5.9) * mm, "radius": 1.02 * mm});
            skCircle(sketch, "E249", {"center": v(19.71, 5.9) * mm, "radius": 1.02 * mm});
            skCircle(sketch, "E250", {"center": v(24.82, 5.9) * mm, "radius": 1.02 * mm});
            skSolve(sketch);
        }
        {
            var Q0;
            Q0 = qSketchRegion(id + "F18", true);
            extrude(context, id + "F19", {"entities" : qUnion([Q0]), "operationType" : NewBodyOperationType.ADD, "depth" : 8.9 * mm, "offsetDistance" : 25.4 * mm});
        }
        {
            var Q0;
            Q0=makeQuery(id+"F1.opExtrude","CAP_FACE",FACE,{"disambiguationData":[OSD([sQuery(id+"F0.wireOp",EDGE,"E0.bottom"),sQuery(id+"F0.wireOp",EDGE,"E0.top"),sQuery(id+"F0.wireOp",EDGE,"E0.left"),sQuery(id+"F0.wireOp",EDGE,"E0.right")])],"isStart":false});
            var sketch = newSketch(context, id + "F20", { "sketchPlane" : qUnion([Q0])});
            skLineSegment(sketch, "E251.bottom", {"start": v(59.49, 131.32) * mm, "end": v(69.52, 131.32) * mm});
            skLineSegment(sketch, "E251.top", {"start": v(59.49, 125.27) * mm, "end": v(69.52, 125.27) * mm});
            skLineSegment(sketch, "E251.left", {"start": v(59.49, 131.32) * mm, "end": v(59.49, 125.27) * mm});
            skLineSegment(sketch, "E251.right", {"start": v(69.52, 131.32) * mm, "end": v(69.52, 125.27) * mm});
            skLineSegment(sketch, "E252.bottom", {"start": v(59.49, 113.46) * mm, "end": v(69.52, 113.46) * mm});
            skLineSegment(sketch, "E252.top", {"start": v(59.49, 107.42) * mm, "end": v(69.52, 107.42) * mm});
            skLineSegment(sketch, "E252.left", {"start": v(59.49, 113.46) * mm, "end": v(59.49, 107.42) * mm});
            skLineSegment(sketch, "E252.right", {"start": v(69.52, 113.46) * mm, "end": v(69.52, 107.42) * mm});
            skLineSegment(sketch, "E253.bottom", {"start": v(59.49, 91.85) * mm, "end": v(69.52, 91.85) * mm});
            skLineSegment(sketch, "E253.top", {"start": v(59.49, 85.8) * mm, "end": v(69.52, 85.8) * mm});
            skLineSegment(sketch, "E253.left", {"start": v(59.49, 91.85) * mm, "end": v(59.49, 85.8) * mm});
            skLineSegment(sketch, "E253.right", {"start": v(69.52, 91.85) * mm, "end": v(69.52, 85.8) * mm});
            skLineSegment(sketch, "E254.bottom", {"start": v(59.49, 40.34) * mm, "end": v(69.52, 40.34) * mm});
            skLineSegment(sketch, "E254.top", {"start": v(59.49, 34.29) * mm, "end": v(69.52, 34.29) * mm});
            skLineSegment(sketch, "E254.left", {"start": v(59.49, 40.34) * mm, "end": v(59.49, 34.29) * mm});
            skLineSegment(sketch, "E254.right", {"start": v(69.52, 40.34) * mm, "end": v(69.52, 34.29) * mm});
            skLineSegment(sketch, "E255.bottom", {"start": v(41.66, 153.92) * mm, "end": v(51.69, 153.92) * mm});
            skLineSegment(sketch, "E255.top", {"start": v(41.66, 147.88) * mm, "end": v(51.69, 147.88) * mm});
            skLineSegment(sketch, "E255.left", {"start": v(41.66, 153.92) * mm, "end": v(41.66, 147.88) * mm});
            skLineSegment(sketch, "E255.right", {"start": v(51.69, 153.92) * mm, "end": v(51.69, 147.88) * mm});
            skLineSegment(sketch, "E256.bottom", {"start": v(41.66, 143.69) * mm, "end": v(51.69, 143.69) * mm});
            skLineSegment(sketch, "E256.top", {"start": v(41.66, 137.64) * mm, "end": v(51.69, 137.64) * mm});
            skLineSegment(sketch, "E256.left", {"start": v(41.66, 143.69) * mm, "end": v(41.66, 137.64) * mm});
            skLineSegment(sketch, "E256.right", {"start": v(51.69, 143.69) * mm, "end": v(51.69, 137.64) * mm});
            skLineSegment(sketch, "E257.bottom", {"start": v(41.66, 131.01) * mm, "end": v(51.69, 131.01) * mm});
            skLineSegment(sketch, "E257.top", {"start": v(41.66, 124.97) * mm, "end": v(51.69, 124.97) * mm});
            skLineSegment(sketch, "E257.left", {"start": v(41.66, 131.01) * mm, "end": v(41.66, 124.97) * mm});
            skLineSegment(sketch, "E257.right", {"start": v(51.69, 131.01) * mm, "end": v(51.69, 124.97) * mm});
            skLineSegment(sketch, "E258.bottom", {"start": v(41.66, 114.55) * mm, "end": v(51.69, 114.55) * mm});
            skLineSegment(sketch, "E258.top", {"start": v(41.66, 108.5) * mm, "end": v(51.69, 108.5) * mm});
            skLineSegment(sketch, "E258.left", {"start": v(41.66, 114.55) * mm, "end": v(41.66, 108.5) * mm});
            skLineSegment(sketch, "E258.right", {"start": v(51.69, 114.55) * mm, "end": v(51.69, 108.5) * mm});
            skLineSegment(sketch, "E259.bottom", {"start": v(41.66, 103.25) * mm, "end": v(51.69, 103.25) * mm});
            skLineSegment(sketch, "E259.top", {"start": v(41.66, 97.2) * mm, "end": v(51.69, 97.2) * mm});
            skLineSegment(sketch, "E259.left", {"start": v(41.66, 103.25) * mm, "end": v(41.66, 97.2) * mm});
            skLineSegment(sketch, "E259.right", {"start": v(51.69, 103.25) * mm, "end": v(51.69, 97.2) * mm});
            skLineSegment(sketch, "E260.bottom", {"start": v(41.66, 76.45) * mm, "end": v(51.69, 76.45) * mm});
            skLineSegment(sketch, "E260.top", {"start": v(41.66, 70.4) * mm, "end": v(51.69, 70.4) * mm});
            skLineSegment(sketch, "E260.left", {"start": v(41.66, 76.45) * mm, "end": v(41.66, 70.4) * mm});
            skLineSegment(sketch, "E260.right", {"start": v(51.69, 76.45) * mm, "end": v(51.69, 70.4) * mm});
            skLineSegment(sketch, "E261.bottom", {"start": v(41.66, 63.88) * mm, "end": v(51.69, 63.88) * mm});
            skLineSegment(sketch, "E261.top", {"start": v(41.66, 57.84) * mm, "end": v(51.69, 57.84) * mm});
            skLineSegment(sketch, "E261.left", {"start": v(41.66, 63.88) * mm, "end": v(41.66, 57.84) * mm});
            skLineSegment(sketch, "E261.right", {"start": v(51.69, 63.88) * mm, "end": v(51.69, 57.84) * mm});
            skLineSegment(sketch, "E262.bottom", {"start": v(41.66, 49.86) * mm, "end": v(51.69, 49.86) * mm});
            skLineSegment(sketch, "E262.top", {"start": v(41.66, 43.81) * mm, "end": v(51.69, 43.81) * mm});
            skLineSegment(sketch, "E262.left", {"start": v(41.66, 49.86) * mm, "end": v(41.66, 43.81) * mm});
            skLineSegment(sketch, "E262.right", {"start": v(51.69, 49.86) * mm, "end": v(51.69, 43.81) * mm});
            skSolve(sketch);
        }
        {
            var Q0;
            Q0 = qSketchRegion(id + "F20", true);
            extrude(context, id + "F21", {"entities" : qUnion([Q0]), "operationType" : NewBodyOperationType.ADD, "depth" : 5.7 * mm, "offsetDistance" : 25.4 * mm});
        }
        {
            var Q0;
            Q0=makeQuery(id+"F1.opExtrude","CAP_FACE",FACE,{"disambiguationData":[OSD([sQuery(id+"F0.wireOp",EDGE,"E0.bottom"),sQuery(id+"F0.wireOp",EDGE,"E0.top"),sQuery(id+"F0.wireOp",EDGE,"E0.left"),sQuery(id+"F0.wireOp",EDGE,"E0.right")])],"isStart":false});
            var sketch = newSketch(context, id + "F22", { "sketchPlane" : qUnion([Q0])});
            skLineSegment(sketch, "E263.bottom", {"start": v(1.65, 31.75) * mm, "end": v(9.53, 31.75) * mm});
            skLineSegment(sketch, "E263.top", {"start": v(1.65, 36.07) * mm, "end": v(9.53, 36.07) * mm});
            skLineSegment(sketch, "E263.left", {"start": v(1.65, 31.75) * mm, "end": v(1.65, 36.07) * mm});
            skLineSegment(sketch, "E263.right", {"start": v(9.53, 31.75) * mm, "end": v(9.53, 36.07) * mm});
            skLineSegment(sketch, "E264.bottom", {"start": v(1.65, 36.2) * mm, "end": v(9.53, 36.2) * mm});
            skLineSegment(sketch, "E264.top", {"start": v(1.65, 40.51) * mm, "end": v(9.53, 40.51) * mm});
            skLineSegment(sketch, "E264.left", {"start": v(1.65, 36.2) * mm, "end": v(1.65, 40.51) * mm});
            skLineSegment(sketch, "E264.right", {"start": v(9.52, 36.2) * mm, "end": v(9.52, 40.51) * mm});
            skSolve(sketch);
        }
        {
            var Q0;
            Q0 = qSketchRegion(id + "F22", true);
            extrude(context, id + "F23", {"entities" : qUnion([Q0]), "operationType" : NewBodyOperationType.ADD, "depth" : 9.73 * mm, "offsetDistance" : 25.4 * mm});
        }
        {
            var Q0;
            Q0=makeQuery(id+"F23.opExtrude","SWEPT_FACE",FACE,{"disambiguationData":[OSD([sQuery(id+"F22.wireOp",EDGE,"E263.left")])]});
            var sketch = newSketch(context, id + "F24", { "sketchPlane" : qUnion([Q0])});
            skPoint(sketch, "E265.startSnap0", {"position": v(-33.9, 8.88) * mm});
            skCircle(sketch, "E266", {"center": v(-33.9, 8.88) * mm, "radius": 1.4 * mm});
            skCircle(sketch, "E267", {"center": v(-33.9, 4.02) * mm, "radius": 1.4 * mm});
            skCircle(sketch, "E268", {"center": v(-38.35, 8.88) * mm, "radius": 1.4 * mm});
            skCircle(sketch, "E269", {"center": v(-38.35, 4.02) * mm, "radius": 1.4 * mm});
            skSolve(sketch);
        }
        {
            var Q0;
            Q0 = qSketchRegion(id + "F24", true);
            extrude(context, id + "F25", {"entities" : qUnion([Q0]), "operationType" : NewBodyOperationType.ADD, "depth" : 2.03 * mm, "offsetDistance" : 25.4 * mm});
        }
        {
            var Q0;
            Q0=makeQuery(id+"F25.opExtrude","CAP_EDGE",EDGE,{"disambiguationData":[OSD([sQuery(id+"F24.wireOp",EDGE,"E268")])],"isStart":false});
            var Q1;
            Q1=makeQuery(id+"F25.opExtrude","CAP_EDGE",EDGE,{"disambiguationData":[OSD([sQuery(id+"F24.wireOp",EDGE,"E266")])],"isStart":false});
            var Q2;
            Q2=makeQuery(id+"F25.opExtrude","CAP_EDGE",EDGE,{"disambiguationData":[OSD([sQuery(id+"F24.wireOp",EDGE,"E267")])],"isStart":false});
            var Q3;
            Q3=makeQuery(id+"F25.opExtrude","CAP_EDGE",EDGE,{"disambiguationData":[OSD([sQuery(id+"F24.wireOp",EDGE,"E269")])],"isStart":false});
            fillet(context, id + "F26", {"entities" : qUnion([Q0, Q1, Q2, Q3]), "radius" : 0.76 * mm, "tangentPropagation" : true, "allowEdgeOverflow" : false});
        }
    });
